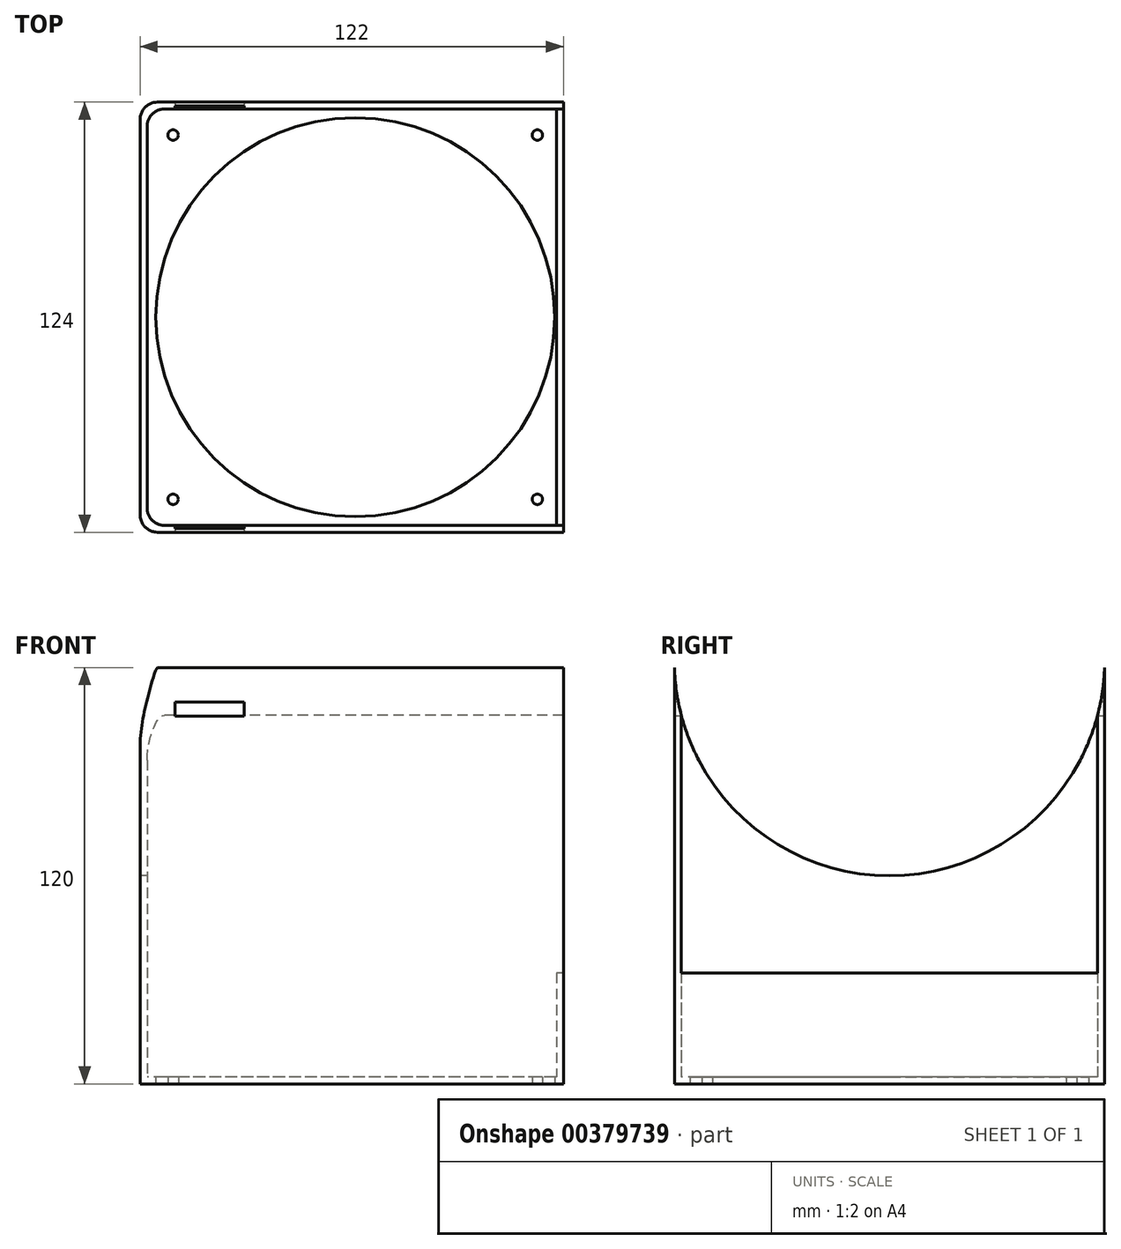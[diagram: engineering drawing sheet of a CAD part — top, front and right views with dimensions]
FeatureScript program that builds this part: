
annotation { "Feature Type Name" : "Feature", "Feature Type Description" : "" }
export const myFeature = defineFeature(function(context is Context, id is Id, definition is map)
    precondition{}
    {
        {
            var Q0;
            Q0=qCreatedBy(makeId("Top.planeOp"),FACE);
            var sketch = newSketch(context, id + "F0", { "sketchPlane" : qUnion([Q0])});
            skLineSegment(sketch, "E0.bottom", {"start": v(60, -60) * mm, "end": v(-60, -60) * mm});
            skLineSegment(sketch, "E0.top", {"start": v(60, 60) * mm, "end": v(-60, 60) * mm});
            skLineSegment(sketch, "E0.left", {"start": v(60, -60) * mm, "end": v(60, 60) * mm});
            skLineSegment(sketch, "E0.right", {"start": v(-60, -60) * mm, "end": v(-60, 60) * mm});
            skPoint(sketch, "E0.middle", {"position": v(0, 0) * mm});
            skCircle(sketch, "E1", {"center": v(0, 0) * mm, "radius": 57.5 * mm});
            skPoint(sketch, "E2", {"position": v(-52.5, 52.5) * mm});
            skPoint(sketch, "E3", {"position": v(52.5, 52.5) * mm});
            skPoint(sketch, "E4", {"position": v(52.5, -52.5) * mm});
            skPoint(sketch, "E5", {"position": v(-52.5, -52.5) * mm});
            skLineSegment(sketch, "E6.0", {"start": v(62, 62) * mm, "end": v(-62, 62) * mm});
            skLineSegment(sketch, "E6.1", {"start": v(62, -62) * mm, "end": v(62, 62) * mm});
            skLineSegment(sketch, "E6.2", {"start": v(62, -62) * mm, "end": v(-62, -62) * mm});
            skLineSegment(sketch, "E6.3", {"start": v(-62, -62) * mm, "end": v(-62, 62) * mm});
            skLineSegment(sketch, "E7", {"start": v(60, 60) * mm, "end": v(60, 62) * mm});
            skLineSegment(sketch, "E8", {"start": v(60, -60) * mm, "end": v(60, -62) * mm});
            skSolve(sketch);
        }
        {
            var Q0;
            Q0=makeQuery(id+"F0.imprint","IMPRINT",FACE,{"disambiguationData":[TD([[makeQuery(id+"F0.imprint","IMPRINT",EDGE,{"derivedFrom":sQuery(id+"F0.wireOp",EDGE,"E0.bottom")}),-1.0]])]});
            extrude(context, id + "F1", {"entities" : qUnion([Q0]), "depth" : 2 * mm});
        }
        {
            var Q0;
            Q0=makeQuery(id+"F0.imprint","IMPRINT",FACE,{"disambiguationData":[TD([[makeQuery(id+"F0.imprint","IMPRINT",EDGE,{"derivedFrom":sQuery(id+"F0.wireOp",EDGE,"E0.bottom")}),1.0]])]});
            extrude(context, id + "F2", {"entities" : qUnion([Q0]), "operationType" : NewBodyOperationType.ADD, "depth" : 120 * mm});
        }
        {
            var Q0;
            Q0=sQuery(id+"F0.wireOp",VERTEX,"E4");
            var Q1;
            Q1=sQuery(id+"F0.wireOp",VERTEX,"E3");
            var Q2;
            Q2=sQuery(id+"F0.wireOp",VERTEX,"E2");
            var Q3;
            Q3=sQuery(id+"F0.wireOp",VERTEX,"E5");
            var Q4;
            Q4=makeQuery(id+"F1.opExtrude","SWEPT_BODY",BODY,{"disambiguationData":[OSD([sQuery(id+"F0.wireOp",EDGE,"E0.bottom"),sQuery(id+"F0.wireOp",EDGE,"E0.top"),sQuery(id+"F0.wireOp",EDGE,"E0.left"),sQuery(id+"F0.wireOp",EDGE,"E0.right"),sQuery(id+"F0.wireOp",EDGE,"E1")])]});
            hole(context, id + "F3", {"style" : HoleStyle.SIMPLE, "endStyle" : HoleEndStyle.THROUGH, "oppositeDirection" : true, "holeDiameter" : 3 * mm, "isTappedThrough" : true, "tappedDepth" : 12 * mm, "tapClearance" : 3, "locations" : qUnion([Q0, Q1, Q2, Q3]), "scope" : qUnion([Q4])});
        }
        {
            var Q0;
            Q0=makeQuery(id+"F2.opExtrude","SWEPT_FACE",FACE,{"disambiguationData":[OSD([sQuery(id+"F0.wireOp",EDGE,"E6.3")])]});
            var sketch = newSketch(context, id + "F4", { "sketchPlane" : qUnion([Q0])});
            skArc(sketch, "E9", {"start": v(-62, 120) * mm, "mid": v(0, 60) * mm, "end": v(62, 120) * mm});
            skSolve(sketch);
        }
        {
            var Q0;
            Q0=makeQuery(id+"F4.imprint","IMPRINT",FACE,{"disambiguationData":[TD([[makeQuery(id+"F4.imprint","IMPRINT",EDGE,{"derivedFrom":sQuery(id+"F4.wireOp",EDGE,"E9")}),1.0]])]});
            extrude(context, id + "F5", {"entities" : qUnion([Q0]), "operationType" : NewBodyOperationType.REMOVE, "endBound" : BoundingType.UP_TO_NEXT, "oppositeDirection" : true, "depth" : 25 * mm});
        }
        {
            var Q0;
            Q0=makeQuery(id+"F2.opExtrude","SWEPT_FACE",FACE,{"disambiguationData":[OSD([sQuery(id+"F0.wireOp",EDGE,"E6.2")])]});
            var sketch = newSketch(context, id + "F6", { "sketchPlane" : qUnion([Q0])});
            skLineSegment(sketch, "E10.bottom", {"start": v(-52, 110) * mm, "end": v(-32, 110) * mm});
            skLineSegment(sketch, "E10.top", {"start": v(-52, 106) * mm, "end": v(-32, 106) * mm});
            skLineSegment(sketch, "E10.left", {"start": v(-52, 110) * mm, "end": v(-52, 106) * mm});
            skLineSegment(sketch, "E10.right", {"start": v(-32, 110) * mm, "end": v(-32, 106) * mm});
            skSolve(sketch);
        }
        {
            var Q0;
            Q0=makeQuery(id+"F6.imprint","IMPRINT",FACE,{"disambiguationData":[TD([[makeQuery(id+"F6.imprint","IMPRINT",EDGE,{"derivedFrom":sQuery(id+"F6.wireOp",EDGE,"E10.bottom")}),-1.0]])]});
            extrude(context, id + "F7", {"entities" : qUnion([Q0]), "operationType" : NewBodyOperationType.REMOVE, "endBound" : BoundingType.THROUGH_ALL, "oppositeDirection" : true, "depth" : 25 * mm});
        }
        {
            var Q0;
            Q0=makeQuery(id+"F1.opExtrude","CAP_FACE",FACE,{"disambiguationData":[OSD([sQuery(id+"F0.wireOp",EDGE,"E0.bottom"),sQuery(id+"F0.wireOp",EDGE,"E0.top"),sQuery(id+"F0.wireOp",EDGE,"E0.left"),sQuery(id+"F0.wireOp",EDGE,"E0.right"),sQuery(id+"F0.wireOp",EDGE,"E1")])],"isStart":false});
            var sketch = newSketch(context, id + "F8", { "sketchPlane" : qUnion([Q0])});
            skLineSegment(sketch, "E11", {"start": v(58, 60) * mm, "end": v(58, -60) * mm});
            skSolve(sketch);
        }
        {
            var Q0;
            {var subQ0=sQuery(id+"F8.wireOp",EDGE,"E11");Q0=makeQuery(id+"F8.imprint","IMPRINT",FACE,{"disambiguationData":[TD([[makeQuery(id+"F8.imprint","IMPRINT",EDGE,{"derivedFrom":subQ0}),1.0]])]});}
            extrude(context, id + "F9", {"entities" : qUnion([Q0]), "operationType" : NewBodyOperationType.ADD, "depth" : 30 * mm});
        }
        {
            var Q0;
            Q0=makeQuery(id+"F9.opExtrude","CAP_EDGE",EDGE,{"disambiguationData":[OSD([sQuery(id+"F0.wireOp",EDGE,"E0.top")])],"isStart":false});
            var Q1;
            Q1=makeQuery(id+"F9.opExtrude","CAP_EDGE",EDGE,{"disambiguationData":[OSD([sQuery(id+"F0.wireOp",EDGE,"E0.bottom")])],"isStart":false});
            var Q2;
            Q2=makeQuery(id+"F2.opExtrude","SWEPT_EDGE",EDGE,{"disambiguationData":[OSD([sQuery(id+"F0.wireOp",EDGE,"E0.bottom"),sQuery(id+"F0.wireOp",EDGE,"E0.right")])]});
            var Q3;
            Q3=makeQuery(id+"F2.opExtrude","SWEPT_EDGE",EDGE,{"disambiguationData":[OSD([sQuery(id+"F0.wireOp",EDGE,"E6.2"),sQuery(id+"F0.wireOp",EDGE,"E6.3")])]});
            var Q4;
            Q4=makeQuery(id+"F2.opExtrude","SWEPT_EDGE",EDGE,{"disambiguationData":[OSD([sQuery(id+"F0.wireOp",EDGE,"E6.0"),sQuery(id+"F0.wireOp",EDGE,"E6.3")])]});
            var Q5;
            Q5=makeQuery(id+"F2.opExtrude","SWEPT_EDGE",EDGE,{"disambiguationData":[OSD([sQuery(id+"F0.wireOp",EDGE,"E0.top"),sQuery(id+"F0.wireOp",EDGE,"E0.right")])]});
            fillet(context, id + "F10", {"entities" : qUnion([Q0, Q1, Q2, Q3, Q4, Q5]), "radius" : 5 * mm, "tangentPropagation" : true, "allowEdgeOverflow" : false});
        }
    });
